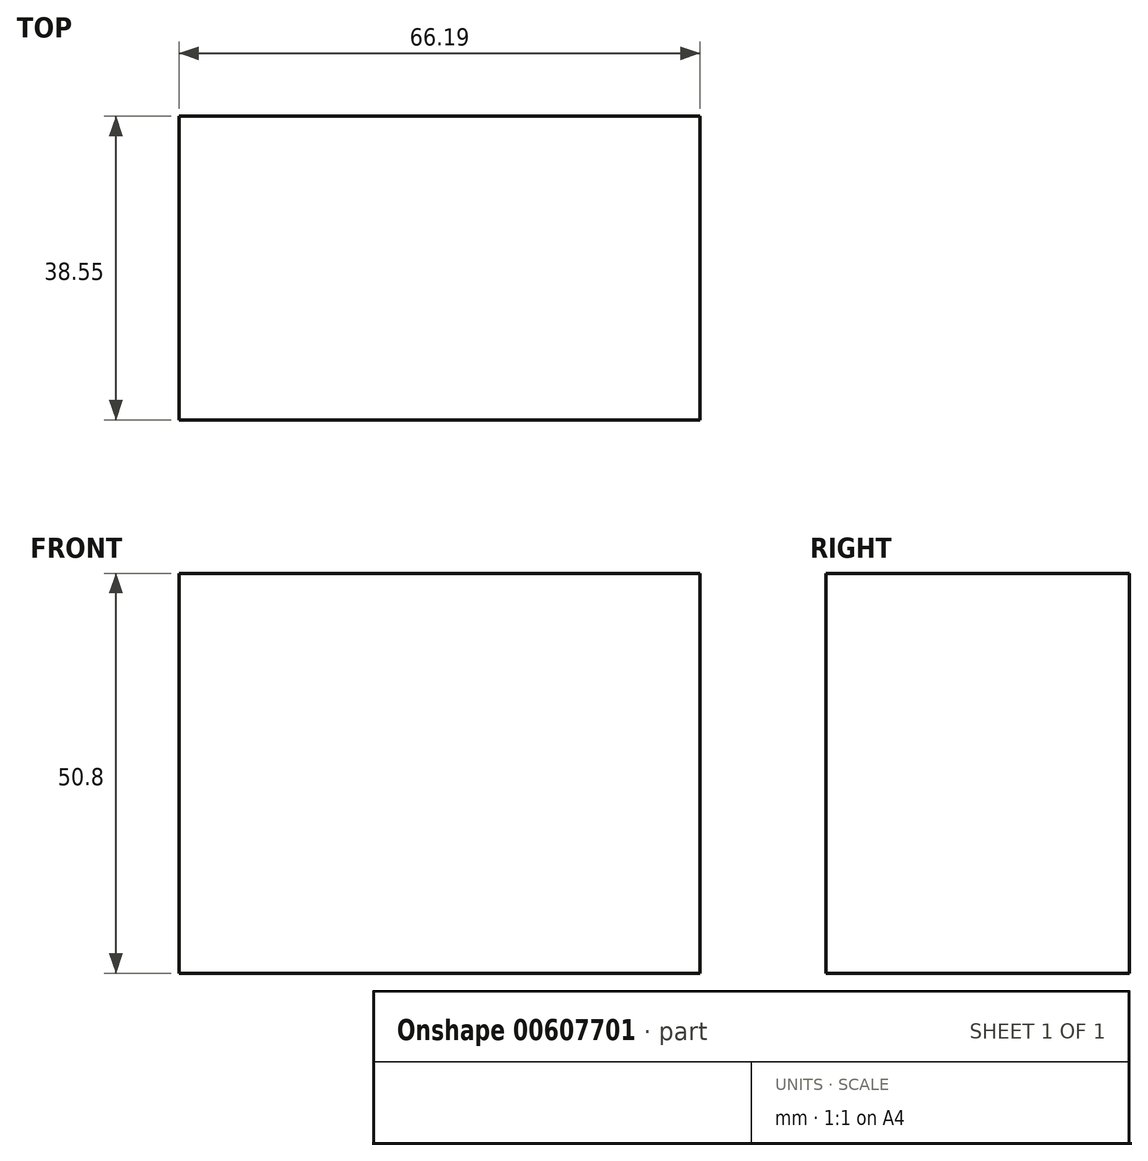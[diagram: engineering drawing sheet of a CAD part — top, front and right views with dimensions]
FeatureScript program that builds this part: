
annotation { "Feature Type Name" : "Feature", "Feature Type Description" : "" }
export const myFeature = defineFeature(function(context is Context, id is Id, definition is map)
    precondition{}
    {
        {
            var Q0;
            Q0=qCreatedBy(makeId("Top.planeOp"),FACE);
            var sketch = newSketch(context, id + "F0", { "sketchPlane" : qUnion([Q0])});
            skLineSegment(sketch, "E0.bottom", {"start": v(-39.97, 17.24) * mm, "end": v(26.22, 17.24) * mm});
            skLineSegment(sketch, "E0.top", {"start": v(-39.97, -21.3) * mm, "end": v(26.22, -21.3) * mm});
            skLineSegment(sketch, "E0.left", {"start": v(-39.97, 17.24) * mm, "end": v(-39.97, -21.3) * mm});
            skLineSegment(sketch, "E0.right", {"start": v(26.22, 17.24) * mm, "end": v(26.22, -21.3) * mm});
            skSolve(sketch);
        }
        {
            var Q0;
            Q0=makeQuery(id+"F0.imprint","IMPRINT",FACE,{"disambiguationData":[TD([[makeQuery(id+"F0.imprint","IMPRINT",EDGE,{"derivedFrom":sQuery(id+"F0.wireOp",EDGE,"E0.bottom")}),-1.0]])]});
            extrude(context, id + "F1", {"entities" : qUnion([Q0]), "depth" : 50.8 * mm, "offsetDistance" : 25.4 * mm});
        }
    });
